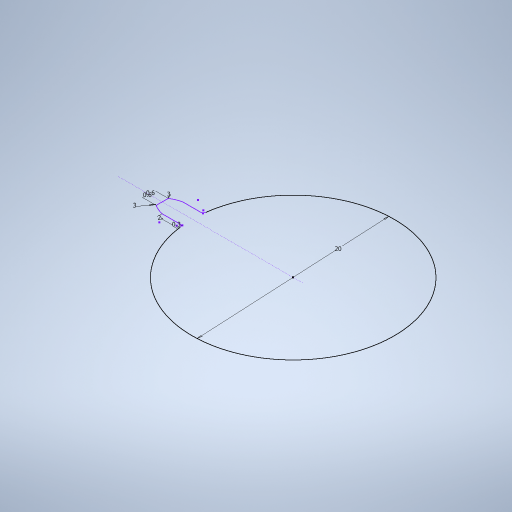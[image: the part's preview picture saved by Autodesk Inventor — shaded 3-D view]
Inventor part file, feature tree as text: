
AUTODESK INVENTOR PART (.ipt)
format: ipt  version: 2024 (Build 280153000, 153)  size: 240,128 bytes
history: native  units: in
note: dims shown in document units (in); Inventor stores cm internally (conversion verified against a paired STEP export)
features: sketch x1
ambient origin geometry x8: Origin, YZ Plane, XZ Plane, XY Plane, X Axis, Y Axis, Z Axis, Center Point
feature tree (1):
  sketch  "Sketch3"  dims[d0=0.7874in d24=0.315in d31=0.1969in d34=0.7874in d39=0.0236in d40=0.0236in d41=0.1181in d42=0.1181in d43=0.0787in d44=0.0118in]
